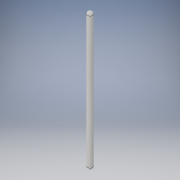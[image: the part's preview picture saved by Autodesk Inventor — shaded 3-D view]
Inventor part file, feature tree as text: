
AUTODESK INVENTOR PART (.ipt)
format: ipt  version: 2019 (Build 230136000, 136)  size: 94,208 bytes
history: native  units: in
note: dims shown in document units (in); Inventor stores cm internally (conversion verified against a paired STEP export)
features: extrude x1, fillet x1, sketch x1
ambient origin geometry x8: Origin, YZ Plane, XZ Plane, XY Plane, X Axis, Y Axis, Z Axis, Center Point
bodies: Solid1 (feature_tree)
feature tree (3):
  extrude  "Extrusion1"  Depth=0.064in TaperAngle=0.0deg
  fillet  "Fillet1"  Radius=0.064in
  sketch  "Sketch1"  dims[d0=0.128in d1=3.327in d2=0.0in d3=0.064in]
